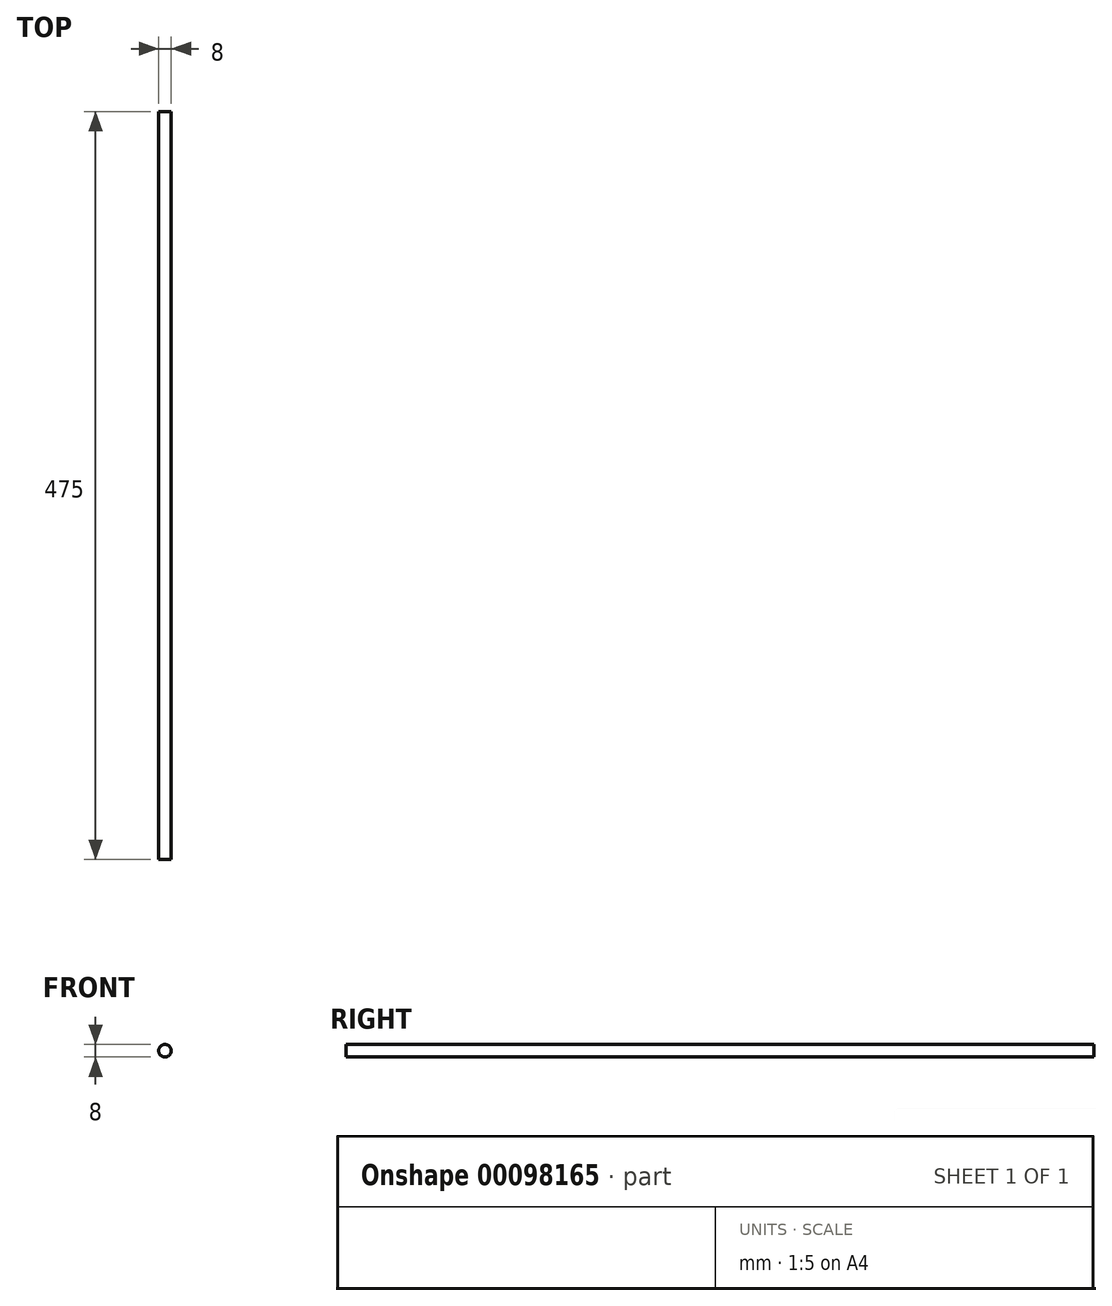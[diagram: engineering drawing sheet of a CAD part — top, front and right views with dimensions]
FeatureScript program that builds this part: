
annotation { "Feature Type Name" : "Feature", "Feature Type Description" : "" }
export const myFeature = defineFeature(function(context is Context, id is Id, definition is map)
    precondition{}
    {
        {
            var Q0;
            Q0=qCreatedBy(makeId("Front.planeOp"),FACE);
            var sketch = newSketch(context, id + "F0", { "sketchPlane" : qUnion([Q0])});
            skCircle(sketch, "E0", {"center": v(0, 0) * mm, "radius": 4 * mm});
            skSolve(sketch);
        }
        {
            var Q0;
            Q0=makeQuery(id+"F0.imprint","IMPRINT",FACE,{"disambiguationData":[TD([[makeQuery(id+"F0.imprint","IMPRINT",EDGE,{"derivedFrom":sQuery(id+"F0.wireOp",EDGE,"E0")}),1.0]])]});
            extrude(context, id + "F1", {"entities" : qUnion([Q0]), "depth" : 475 * mm});
        }
    });
